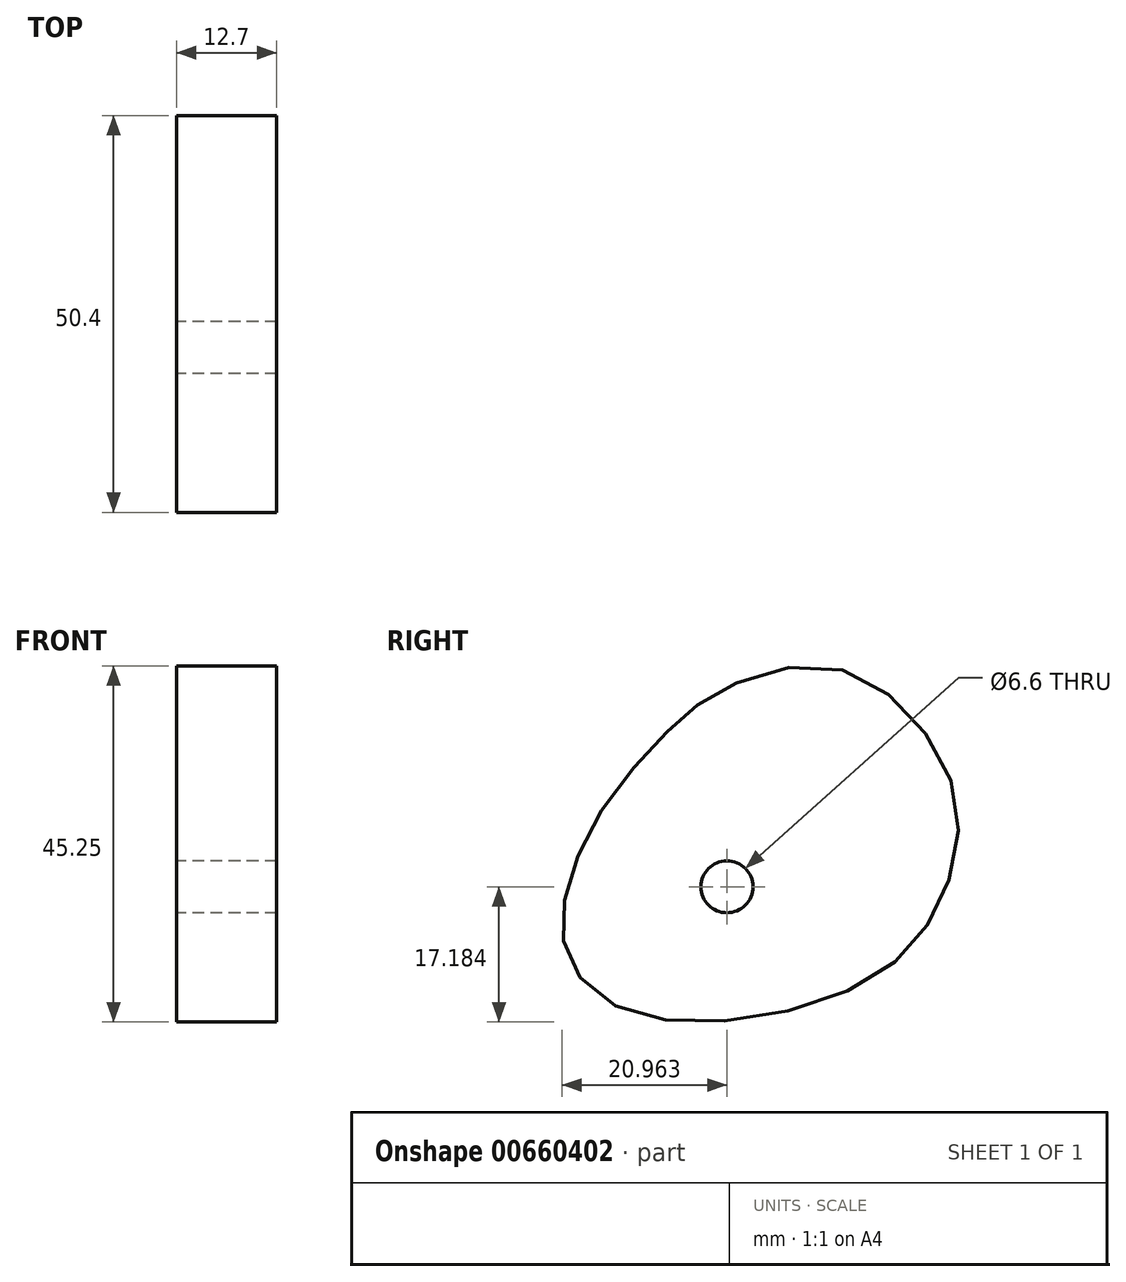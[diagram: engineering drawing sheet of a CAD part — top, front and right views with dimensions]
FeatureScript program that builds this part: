
annotation { "Feature Type Name" : "Feature", "Feature Type Description" : "" }
export const myFeature = defineFeature(function(context is Context, id is Id, definition is map)
    precondition{}
    {
        {
            var Q0;
            Q0=qCreatedBy(makeId("Right.planeOp"),FACE);
            var sketch = newSketch(context, id + "F0", { "sketchPlane" : qUnion([Q0])});
            skFitSpline(sketch, "E0", {"points": [v(-12.9, -4.93) * mm, v(-21.2, -14.79) * mm, v(-25.86, -25.68) * mm, v(-25.6, -33.47) * mm, v(-19.12, -39.95) * mm, v(-3.81, -41.5) * mm, v(13.83, -35.8) * mm, v(21.61, -26.72) * mm, v(23.95, -14.79) * mm, v(17.98, -2.85) * mm, v(6.57, 3.37) * mm, v(-6.66, 0) * mm, v(-12.9, -4.93) * mm]});
            skCircle(sketch, "E1", {"center": v(-5.37, -24.65) * mm, "radius": 3.3 * mm});
            skSolve(sketch);
        }
        {
            var Q0;
            Q0=makeQuery(id+"F0.imprint","IMPRINT",FACE,{"disambiguationData":[TD([[makeQuery(id+"F0.imprint","IMPRINT",EDGE,{"derivedFrom":sQuery(id+"F0.wireOp",EDGE,"E0")}),1.0]])]});
            extrude(context, id + "F1", {"entities" : qUnion([Q0]), "depth" : 12.7 * mm, "offsetDistance" : 25.4 * mm});
        }
    });
